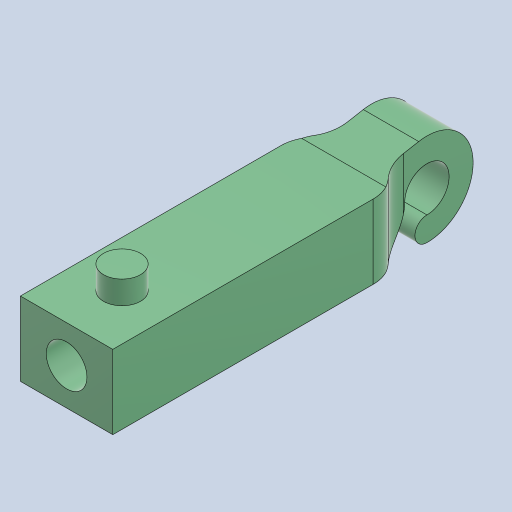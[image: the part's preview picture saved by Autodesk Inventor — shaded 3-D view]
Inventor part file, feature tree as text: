
AUTODESK INVENTOR PART (.ipt)
format: ipt  version: 2023 (Build 270158000, 158)  size: 180,736 bytes
history: native  units: mm
features: sketch x5, extrude x3, hole x2, other x1, fillet x1
ambient origin geometry x8: Origin, YZ Plane, XZ Plane, XY Plane, X Axis, Y Axis, Z Axis, Center Point
bodies: Body1 (feature_tree)
feature tree (12):
  other  "ソリッド1"
  extrude  "押し出し1"  Depth=5.0mm
  extrude  "押し出し2"  Depth=4.0mm TaperAngle=0.0deg
  hole  "加工用"  [1 undecoded]
  extrude  "押し出し4"  Depth=6.5mm TaperAngle=0.0deg
  fillet  "フィレット1"  Radius=15.0mm
  hole  "穴3"  [1 undecoded]
  sketch  "スケッチ1"
  sketch  "スケッチ2"
  sketch  "スケッチ5"
  sketch  "スケッチ6"
  sketch  "スケッチ8"
note: 2 required parameter values undecoded (feature->parameter linkage not recoverable at this tier; creation-order binding heuristic only, values carry confidence <= 0.55)
